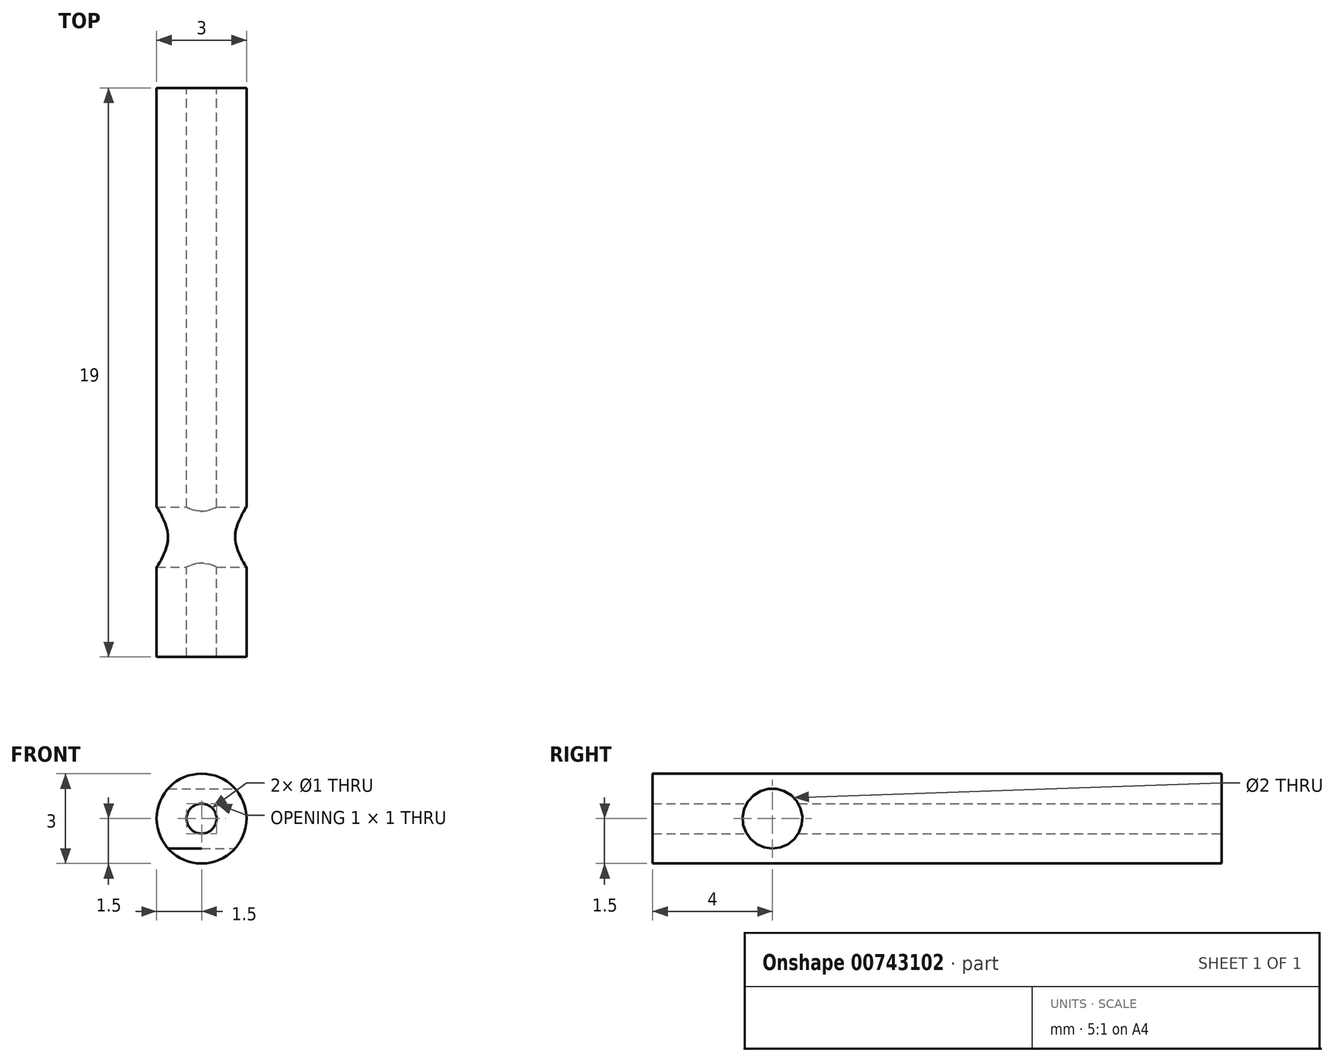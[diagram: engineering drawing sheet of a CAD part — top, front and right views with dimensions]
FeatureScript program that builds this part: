
annotation { "Feature Type Name" : "Feature", "Feature Type Description" : "" }
export const myFeature = defineFeature(function(context is Context, id is Id, definition is map)
    precondition{}
    {
        {
            var Q0;
            Q0=qCreatedBy(makeId("Front.planeOp"),FACE);
            var sketch = newSketch(context, id + "F0", { "sketchPlane" : qUnion([Q0])});
            skCircle(sketch, "E0", {"center": v(0, 0) * mm, "radius": 1.5 * mm});
            skCircle(sketch, "E1.0", {"center": v(0, 0) * mm, "radius": 0.5 * mm});
            skSolve(sketch);
        }
        {
            var Q0;
            Q0=qSketchRegion(id+"F0",true);
            extrude(context, id + "F1", {"entities" : qUnion([Q0]), "depth" : 19 * mm, "offsetDistance" : 25 * mm});
        }
        {
            var Q0;
            Q0=qCreatedBy(makeId("Right.planeOp"),FACE);
            var sketch = newSketch(context, id + "F2", { "sketchPlane" : qUnion([Q0])});
            skCircle(sketch, "E2", {"center": v(-15, 0) * mm, "radius": 1 * mm});
            skSolve(sketch);
        }
        {
            var Q0;
            Q0=qSketchRegion(id+"F2",true);
            extrude(context, id + "F3", {"entities" : qUnion([Q0]), "operationType" : NewBodyOperationType.REMOVE, "endBound" : BoundingType.SYMMETRIC, "oppositeDirection" : true, "depth" : 25 * mm, "offsetDistance" : 25 * mm});
        }
    });
